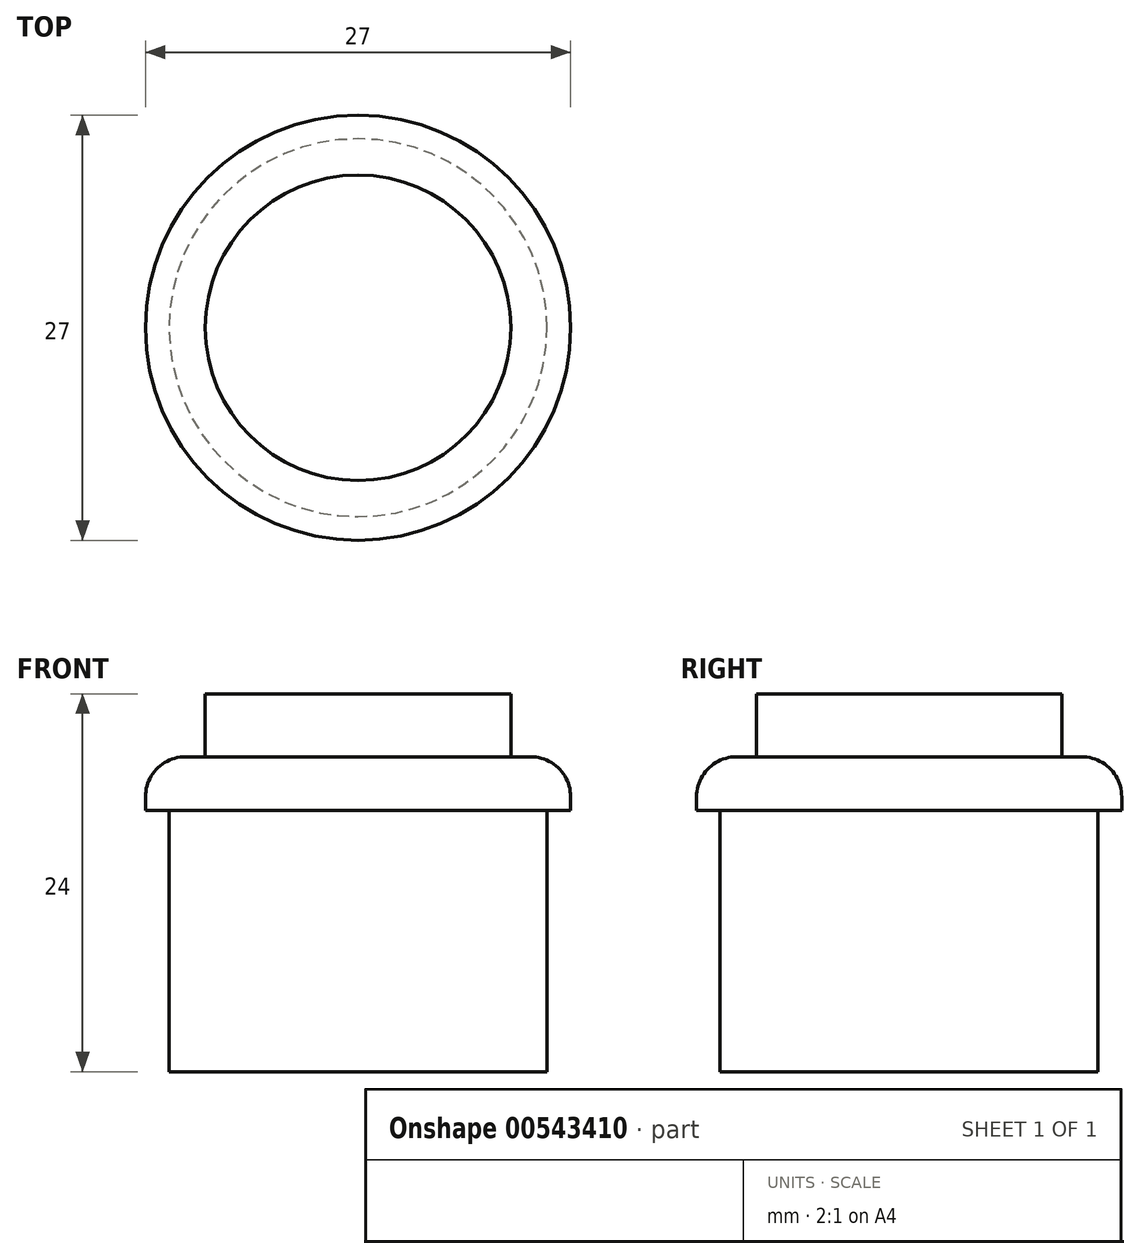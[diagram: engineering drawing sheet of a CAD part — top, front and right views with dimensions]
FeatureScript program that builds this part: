
annotation { "Feature Type Name" : "Feature", "Feature Type Description" : "" }
export const myFeature = defineFeature(function(context is Context, id is Id, definition is map)
    precondition{}
    {
        {
            var Q0;
            Q0=qCreatedBy(makeId("Front.planeOp"),FACE);
            var sketch = newSketch(context, id + "F0", { "sketchPlane" : qUnion([Q0])});
            skLineSegment(sketch, "E0", {"start": v(0, 7.4) * mm, "end": v(9.7, 7.4) * mm});
            skLineSegment(sketch, "E1", {"start": v(9.7, 7.4) * mm, "end": v(9.7, 3.4) * mm});
            skLineSegment(sketch, "E2", {"start": v(9.7, 3.4) * mm, "end": v(13.5, 3.4) * mm});
            skLineSegment(sketch, "E3", {"start": v(13.5, 3.4) * mm, "end": v(13.5, 0) * mm});
            skLineSegment(sketch, "E4", {"start": v(13.5, 0) * mm, "end": v(12, 0) * mm});
            skLineSegment(sketch, "E5", {"start": v(12, 0) * mm, "end": v(12, -16.6) * mm});
            skLineSegment(sketch, "E6", {"start": v(12, -16.6) * mm, "end": v(0, -16.6) * mm});
            skLineSegment(sketch, "E7", {"start": v(0, -16.6) * mm, "end": v(0, 7.4) * mm, "construction": true});
            skLineSegment(sketch, "E8", {"start": v(0, 7.4) * mm, "end": v(0, -16.6) * mm});
            skSolve(sketch);
        }
        {
            var Q0;
            Q0=qSketchRegion(id+"F0",true);
            var Q1;
            Q1=sQuery(id+"F0.wireOp",EDGE,"E8");
            revolve(context, id + "F1", {"entities" : qUnion([Q0]), "axis" : qUnion([Q1]), "revolveType" : RevolveType.FULL});
        }
        {
            var Q0;
            Q0=makeQuery(id+"F1.opRevolve","SWEPT_EDGE",EDGE,{"disambiguationData":[OSD([sQuery(id+"F0.wireOp",EDGE,"E2"),sQuery(id+"F0.wireOp",EDGE,"E3")])]});
            fillet(context, id + "F2", {"entities" : qUnion([Q0]), "radius" : 2.54 * mm, "tangentPropagation" : true, "allowEdgeOverflow" : false});
        }
    });
